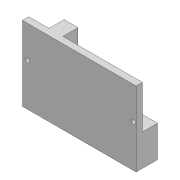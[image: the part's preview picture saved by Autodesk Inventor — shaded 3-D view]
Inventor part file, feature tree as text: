
AUTODESK INVENTOR PART (.ipt)
format: ipt  version: 2018 (Build 220112000, 112)  size: 103,424 bytes
history: native  units: mm
features: sketch x3, extrude x2, hole x1
ambient origin geometry x8: Origin, YZ Plane, XZ Plane, XY Plane, X Axis, Y Axis, Z Axis, Center Point
bodies: Solid1 (feature_tree)
feature tree (6):
  extrude  "Extrusion1"  Depth=90.0mm
  extrude  "Extrusion2"  Depth=25.0mm
  hole  "Hole1"  [1 undecoded]
  sketch  "Sketch1"  dims[d0=59.0mm d1=90.0mm]
  sketch  "Sketch2"  dims[d2=17.0mm d3=0.0mm d4=25.0mm]
  sketch  "Sketch3"  dims[d5=25.0mm d6=16.0mm d7=63.0mm d8=12.0mm d9=0.0mm d10=4.0mm d11=2.0mm d12=25.4mm d13=3.2mm d14=6.0mm d15=6.3mm d16=2.0mm d17=90.0deg d18=8.0mm d19=20.594885mm]
note: 1 required parameter value undecoded (feature->parameter linkage not recoverable at this tier; creation-order binding heuristic only, values carry confidence <= 0.55)
